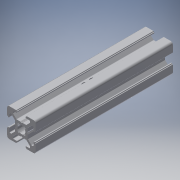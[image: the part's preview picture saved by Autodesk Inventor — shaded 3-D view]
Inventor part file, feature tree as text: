
AUTODESK INVENTOR PART (.ipt)
format: ipt  version: 2016 (Build 200138000, 138)  size: 411,136 bytes
history: native  units: in
note: dims shown in document units (in); Inventor stores cm internally (conversion verified against a paired STEP export)
features: other x3, sketch x2, extrude x1, hole x1, mirror x1
ambient origin geometry x8: Origin, YZ Plane, XZ Plane, XY Plane, X Axis, Y Axis, Z Axis, Center Point
bodies: Solid1 (feature_tree)
feature tree (8):
  other  "Blocks"
  extrude  "Extrusion1"  Depth=2.0in
  hole  "Hole1"  [1 undecoded]
  mirror  "Mirror1"
  sketch  "Sketch1"  dims[d1=0.0in d5=2.0in]
  other  "20x20"
  sketch  "Sketch3"  dims[d6=0.187in d7=0.75in d8=0.375in d9=0.25in d10=0.5635in d11=1.0in d12=0.8108in d13=1.0in d14=1.0in]
  other  "20x20:1"
note: 1 required parameter value undecoded (feature->parameter linkage not recoverable at this tier; creation-order binding heuristic only, values carry confidence <= 0.55)
